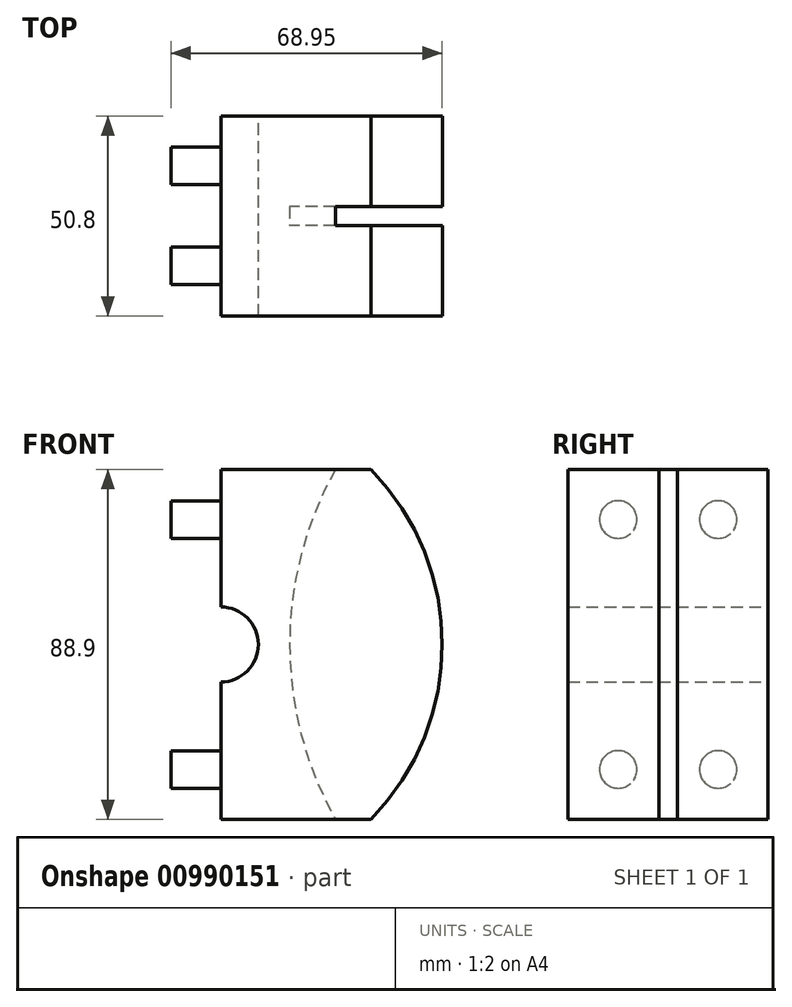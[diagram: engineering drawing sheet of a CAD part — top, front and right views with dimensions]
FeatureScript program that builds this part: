
annotation { "Feature Type Name" : "Feature", "Feature Type Description" : "" }
export const myFeature = defineFeature(function(context is Context, id is Id, definition is map)
    precondition{}
    {
        {
            var Q0;
            Q0=qCreatedBy(makeId("Front.planeOp"),FACE);
            var sketch = newSketch(context, id + "F0", { "sketchPlane" : qUnion([Q0])});
            skLineSegment(sketch, "E0", {"start": v(0, -44.45) * mm, "end": v(0, -9.53) * mm});
            skLineSegment(sketch, "E1", {"start": v(0, 44.45) * mm, "end": v(38.1, 44.45) * mm});
            skLineSegment(sketch, "E2", {"start": v(0, -44.45) * mm, "end": v(38.1, -44.45) * mm});
            skArc(sketch, "E3", {"start": v(38.1, -44.45) * mm, "mid": v(56.25, 0) * mm, "end": v(38.1, 44.45) * mm});
            skArc(sketch, "E4", {"start": v(0, -9.53) * mm, "mid": v(9.53, 0) * mm, "end": v(0, 9.53) * mm});
            skLineSegment(sketch, "E5.trimOffspring", {"start": v(0, 9.53) * mm, "end": v(0, 44.45) * mm});
            skCircle(sketch, "E6", {"center": v(101.6, 0) * mm, "radius": 88.9 * mm, "construction": true});
            skSolve(sketch);
        }
        {
            var Q0;
            Q0=makeQuery(id+"F0.imprint","IMPRINT",FACE,{"disambiguationData":[TD([[makeQuery(id+"F0.imprint","IMPRINT",EDGE,{"derivedFrom":sQuery(id+"F0.wireOp",EDGE,"E0")}),-1.0]])]});
            extrude(context, id + "F1", {"entities" : qUnion([Q0]), "endBound" : BoundingType.SYMMETRIC, "depth" : 50.8 * mm, "offsetDistance" : 25.4 * mm});
        }
        {
            var Q0;
            Q0=qCreatedBy(makeId("Front.planeOp"),FACE);
            var sketch = newSketch(context, id + "F2", { "sketchPlane" : qUnion([Q0])});
            skCircle(sketch, "E7", {"center": v(107.95, 0) * mm, "radius": 90.49 * mm});
            skSolve(sketch);
        }
        {
            var Q0;
            Q0=makeQuery(id+"F2.imprint","IMPRINT",FACE,{"disambiguationData":[TD([[makeQuery(id+"F2.imprint","IMPRINT",EDGE,{"derivedFrom":sQuery(id+"F2.wireOp",EDGE,"E7")}),1.0]])]});
            extrude(context, id + "F3", {"entities" : qUnion([Q0]), "operationType" : NewBodyOperationType.REMOVE, "endBound" : BoundingType.SYMMETRIC, "oppositeDirection" : true, "depth" : 4.76 * mm, "offsetDistance" : 25.4 * mm});
        }
        {
            var Q0;
            Q0=qCreatedBy(makeId("Right.planeOp"),FACE);
            var sketch = newSketch(context, id + "F4", { "sketchPlane" : qUnion([Q0])});
            skCircle(sketch, "E8", {"center": v(12.7, 31.75) * mm, "radius": 4.76 * mm});
            skCircle(sketch, "E9", {"center": v(-12.7, 31.75) * mm, "radius": 4.76 * mm});
            skCircle(sketch, "E10", {"center": v(-12.7, -31.75) * mm, "radius": 4.76 * mm});
            skCircle(sketch, "E11", {"center": v(12.7, -31.75) * mm, "radius": 4.76 * mm});
            skLineSegment(sketch, "E12", {"start": v(12.7, -31.75) * mm, "end": v(12.7, -44.45) * mm, "construction": true});
            skLineSegment(sketch, "E13", {"start": v(12.7, -31.75) * mm, "end": v(25.4, -31.75) * mm, "construction": true});
            skLineSegment(sketch, "E14", {"start": v(-12.7, 44.45) * mm, "end": v(-12.7, 31.75) * mm, "construction": true});
            skLineSegment(sketch, "E15", {"start": v(-25.4, 31.75) * mm, "end": v(-12.7, 31.75) * mm, "construction": true});
            skSolve(sketch);
        }
        {
            var Q0;
            Q0 = qSketchRegion(id + "F4", true);
            extrude(context, id + "F5", {"entities" : qUnion([Q0]), "operationType" : NewBodyOperationType.ADD, "oppositeDirection" : true, "depth" : 12.7 * mm, "offsetDistance" : 25.4 * mm});
        }
    });
